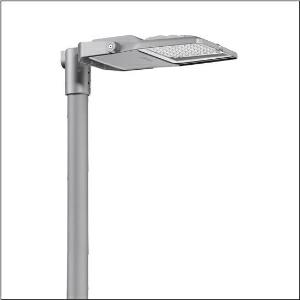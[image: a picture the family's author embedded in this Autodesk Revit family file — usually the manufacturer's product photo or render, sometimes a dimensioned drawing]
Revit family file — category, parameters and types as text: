
# Revit family: floodlight_fl_21_iq_mini___pl43_5xa7772b4a3a_1e53
name_source: partatom
category: Lighting Fixtures
units: mm (PartAtom-declared; Revit-internal decimal feet)

## family parameters
Cut with Voids When Loaded = No
Host = Face
Light Source = No
Part Type = Normal
Room Calculation Point = No
Round Connector Dimension = Use Diameter
Shared = No

## types (1)
- --- (1 x LED, 6660 lm, 45.5 W, 4000K)
    Apparent Load = 46 VA
    CIE Flux Codes = 27 78 99 100 100
    Color Rendering = 70
    Color Temperature = 4000K
    Default Elevation = 1800 mm
    Description = Floodlight FL 21 iQ mini, floodlight, primary light control with lens, of PMMA, primary optical cover: protective disc, of toughened safety glass, transparent, light distribution: PL43, light emission: direct distribution, installation type: surface-mounted, LED, High Power LED, rated luminous flux: 6.660lm, luminous efficacy: 146lm/W, light colour: 740, colour temperature: 4000K, control: Auto-Match, Temp-Guard, Night-Set, Smart-Wire, Desk-Remote (wireless, voltage-free reading and setting of iQ features in the workshop via application-optimized NFC function/RFID function), optimised constant luminous flux control (CLO 2.0), Light-Fading, Lumen-Switch, with terminal, 6-pole, mains connection: 220..240V, AC, 50/60Hz, start of lifetime: 46W, end of service life: 48W, reduction: 22W, luminaire housing, of diecast aluminium, powder-coated, Siteco® metallic grey (DB 702S), corrosivity category C5 mid according to DIN EN ISO 12944, sealing non-destructively replaceable, please order mast flange separately, mast bracket, of steel, galvanised, powder-coated, protection rating (complete): IP66, insulation class (complete): insulation class II (safety insulation), certification: CE, ENEC, VDE, protection symbol: D, impact resistance: IK08, permissible operating ambient temperature: -40..+40°C, permissible operating ambient temperature for outdoor applications: -40..+50°C, standard: DIN EN 12944, LABS conformity tested according to VDMA 24364:2018-05, packaging unit: 1 piece

Light Distribution: PL43
    Height = 70 mm
    Lamp = 1 x LED
    Lamp Light Flux = 6660 lm
    Lamp Power = 45.5 W
    Lamp count = 1
    Length = 485 mm
    Luminous efficacy = 146 lm/W
    Manufacturer = Siteco
    ModVariant = No
    Model = 5XA7772B4A3A
    Number of Poles = 1
    OnlyDefault = Yes
    Power Factor = 1
    Product Name = Floodlight FL 21 iQ mini | PL43
    Product group = floodlight | pylon annexe
    ProductGroupID = 6200
    Protection Class = Protection class II
    Protection Degree = IP 66
    RLX_Detail_Level = 1
    RLX_Emergency_Light_Flux = 0 lm
    RLX_Emergency_Type = 0
    RLX_Emergency_Type_DB = No
    RlxData = <blob elided: 101205 chars, md5=71b70cc6>
    Socket = socket
    Standby Power = 0 W
    System Light Flux = 6660 lm
    System Power = 46 W
    Type Comments = factory setting: luminous flux: 100 % | dim-lin: 254 | 463 mA
    Type Image = l_1007125.jpg
    URL = http://relux.com
    VarID = @adj_094981
    Voltage = 0 V
    Weight = 0.00 kg
    Width = 337 mm

## geometry (parser evidence)
native form markers: Blend x4, Sweep x10
no freeform markers — native parametric forms only
